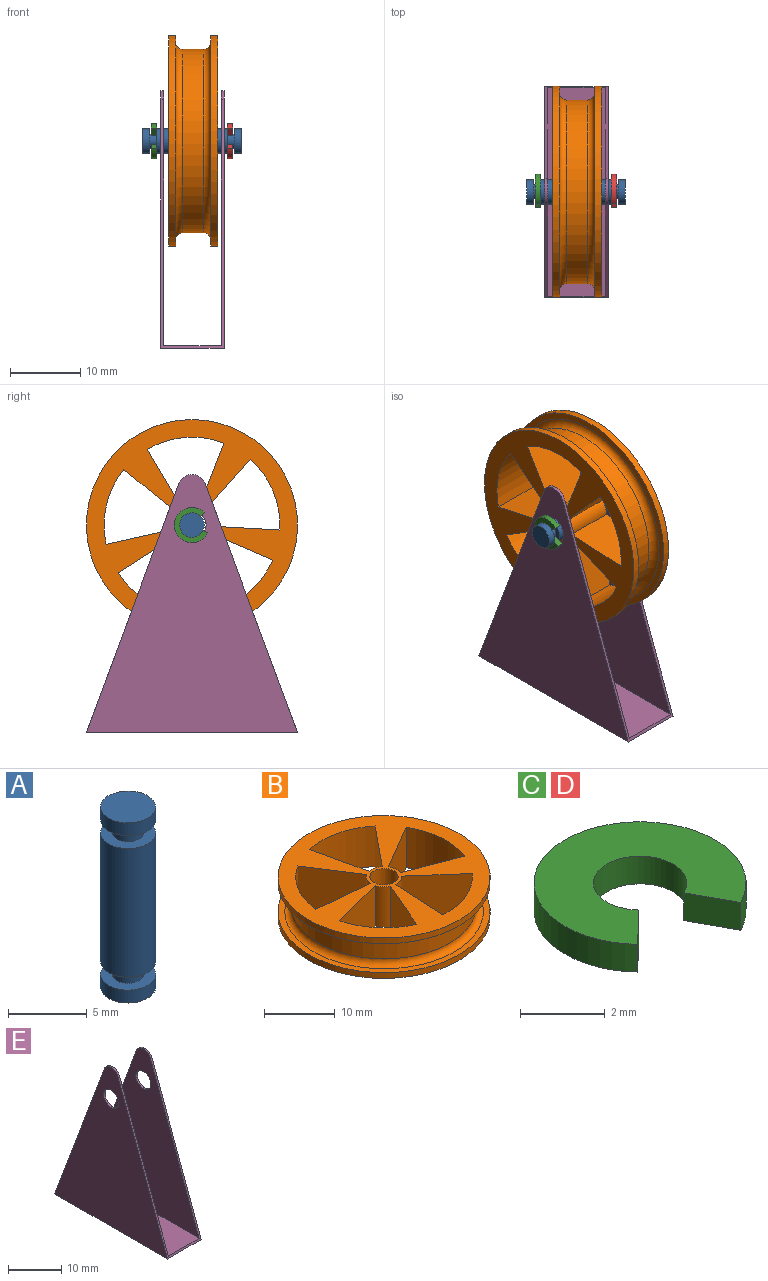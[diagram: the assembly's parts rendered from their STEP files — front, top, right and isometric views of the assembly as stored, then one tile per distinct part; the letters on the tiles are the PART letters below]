
ASSEMBLY  parts=5 mates=6
PART A: 11 faces, bbox 3.5x3.5x14 mm
  f0: cylinder r=1.75mm len=10mm, axis (0,0,-1), area 110mm2, adj f2,f7
  f1: cylinder r=1mm len=2mm, axis (0,0,1), area 6.3mm2, adj f2,f3
  f2: plane 3.5x3.5mm, normal (0,0,1), area 6.5mm2, adj f0,f1
  f3: plane 3.5x3.5mm, normal (0,0,-1), area 6.5mm2, adj f1,f5
  f4: plane 3.5x3.5mm, normal (0,0,1), area 9.6mm2, adj f5
  f5: cylinder r=1.75mm len=3.5mm, axis (0,0,-1), area 11mm2, adj f3,f4
  f6: cylinder r=1mm len=2mm, axis (0,0,-1), area 6.3mm2, adj f7,f8
  f7: plane 3.5x3.5mm, normal (0,0,-1), area 6.5mm2, adj f0,f6
  f8: plane 3.5x3.5mm, normal (0,0,1), area 6.5mm2, adj f6,f10
  f9: plane 3.5x3.5mm, normal (0,0,-1), area 9.6mm2, adj f10
  f10: cylinder r=1.75mm len=3.5mm, axis (0,0,-1), area 11mm2, adj f8,f9
PART B: 30 faces, bbox 31.9x31.9x7 mm
  f0: cylinder r=15mm len=30mm, axis (0,0,-1), area 94.2mm2, adj f23,f25
  f1: cylinder r=2.5mm len=7mm, axis (0,0,-1), area 15.8mm2, adj f2,f21,f22,f23
  f2: plane 7.5x7mm, normal (-0.66,-0.75,0), area 70mm2, adj f1,f3,f22,f23
  f3: cylinder r=12.5mm len=10.07mm, axis (0,0,-1), area 79.1mm2, adj f2,f21,f22,f23
  f4: cylinder r=2.5mm len=7mm, axis (0,0,-1), area 15.8mm2, adj f5,f16,f22,f23
  f5: plane 8.61x7mm, normal (0.51,-0.86,0), area 70mm2, adj f4,f6,f22,f23
  f6: cylinder r=12.5mm len=10.88mm, axis (0,0,-1), area 79.1mm2, adj f5,f16,f22,f23
  f7: cylinder r=12.5mm len=8.28mm, axis (0,0,-1), area 79.1mm2, adj f8,f17,f22,f23
  f8: plane 9.67x7mm, normal (0.26,-0.97,0), area 70mm2, adj f7,f9,f22,f23
  f9: cylinder r=2.5mm len=7mm, axis (0,0,-1), area 15.8mm2, adj f8,f17,f22,f23
  f10: cylinder r=2.5mm len=7mm, axis (0,0,-1), area 15.8mm2, adj f11,f19,f22,f23
  f11: plane 9.76x7mm, normal (0.98,0.22,0), area 70mm2, adj f10,f12,f22,f23
  f12: cylinder r=12.5mm len=10.63mm, axis (0,0,-1), area 79.1mm2, adj f11,f19,f22,f23
  f13: plane 8.41x7mm, normal (-0.84,-0.54,0), area 70mm2, adj f14,f20,f22,f23
  f14: cylinder r=2.5mm len=7mm, axis (0,0,-1), area 15.8mm2, adj f13,f15,f22,f23
  f15: plane 9.96x7mm, normal (0.09,1,0), area 70mm2, adj f14,f20,f22,f23
  f16: plane 9.32x7mm, normal (0.36,0.93,0), area 70mm2, adj f4,f6,f22,f23
  f17: plane 9.18x7mm, normal (-0.92,0.4,0), area 70mm2, adj f7,f9,f22,f23
  f18: cylinder r=15mm len=30mm, axis (0,0,-1), area 94.2mm2, adj f22,f26
  f19: plane 7.75x7mm, normal (-0.78,0.63,0), area 70mm2, adj f10,f12,f22,f23
  f20: cylinder r=12.5mm len=9.33mm, axis (0,0,-1), area 79.1mm2, adj f13,f15,f22,f23
  f21: plane 9.98x7mm, normal (1,-0.06,0), area 70mm2, adj f1,f3,f22,f23
  f22: plane 30x30mm, normal (0,0,1), area 355.3mm2, adj f1,f2,f3,f4,f5,f6,f7,f8
  f23: plane 30x30mm, normal (0,0,-1), area 355.3mm2, adj f0,f1,f2,f3,f4,f5,f6,f7
  f24: cylinder r=13.05mm len=26.1mm, axis (0,0,1), area 245.9mm2, adj f28,f29
  f25: plane 30x30mm, normal (0,0,1), area 86.9mm2, adj f0,f29
  f26: plane 30x30mm, normal (0,0,-1), area 86.9mm2, adj f18,f28
  f27: cylinder r=2mm len=7mm, axis (0,0,1), area 88mm2, adj f22,f23
  f28: torus R=14.05mm, axis (0,0,1), area 132.4mm2, adj f24,f26
  f29: torus R=14.05mm, axis (0,0,1), area 132.4mm2, adj f24,f25
PART C: 6 faces, bbox 5x4.7x0.8 mm
  f0: cylinder r=2.5mm len=5mm, axis (0,0,-1), area 10mm2, adj f1,f2,f4,f5
  f1: plane 5x4.74mm, normal (0,0,1), area 12.7mm2, adj f0,f3,f4,f5
  f2: plane 5x4.74mm, normal (0,0,-1), area 12.7mm2, adj f0,f3,f4,f5
  f3: cylinder r=1.1mm len=2.2mm, axis (0,0,1), area 4.4mm2, adj f1,f2,f4,f5
  f4: plane 1.01x0.97mm, normal (0.69,-0.72,0), area 1.1mm2, adj f0,f1,f2,f3
  f5: plane 1.23x0.8mm, normal (-0.88,-0.48,0), area 1.1mm2, adj f0,f1,f2,f3
PART D: same geometry as C
PART E: 12 faces, bbox 9x30x36.7 mm
  f0: plane 36.25x29.7mm, normal (-1,0,0), area 575.6mm2, adj f2,f3,f4,f5,f7
  f1: plane 36.25x29.7mm, normal (1,0,0), area 575.6mm2, adj f2,f3,f5,f6,f8
  f2: plane 29.7x8.2mm, normal (0,0,1), area 243.6mm2, adj f0,f1,f3,f5
  f3: plane 35.35x13.13mm, normal (0,0.94,0.35), area 33.7mm2, adj f0,f1,f2,f4,f6,f9,f10,f11
  f4: cylinder r=2mm len=3.75mm, axis (-1,0,0), area 1.9mm2, adj f0,f3,f5,f10
  f5: plane 35.35x13.13mm, normal (0,-0.94,0.35), area 33.7mm2, adj f0,f1,f2,f4,f6,f9,f10,f11
  f6: cylinder r=2mm len=3.75mm, axis (-1,0,0), area 1.9mm2, adj f1,f3,f5,f9
  f7: cylinder r=2mm len=4mm, axis (-1,0,0), area 5mm2, adj f0,f10
  f8: cylinder r=2mm len=4mm, axis (-1,0,0), area 5mm2, adj f1,f9
  f9: plane 36.65x30mm, normal (-1,0,0), area 587.5mm2, adj f3,f5,f6,f8,f11
  f10: plane 36.65x30mm, normal (1,0,0), area 587.5mm2, adj f3,f4,f5,f7,f11
  f11: plane 30x9mm, normal (0,0,-1), area 270mm2, adj f3,f5,f9,f10
PLACE A rot(axis=(-0.58,-0.58,0.58),120deg) t=(-4.21,-6.21,9.28)mm
PLACE B rot(axis=(0,-1,0),90deg) t=(-7.55,-6.21,9.28)mm
PLACE C rot(axis=(0,1,0),90deg) t=(-17.01,-6.21,15.86)mm
PLACE D rot(axis=(0,1,0),90deg) t=(-6.21,-6.21,15.86)mm
PLACE E t=(-7.64,-8.5,-20.18)mm
MATE planar A.f0 <-> C.f0  axis (-1,0,0) through (-16.21,-6.21,9.28)mm
MATE planar A.f0 <-> D.f2  axis (1,0,0) through (-6.21,-6.21,9.28)mm
MATE cylindrical A.f0 <-> B.f3  axis (1,0,0) through (-17.71,-6.21,9.28)mm
MATE cylindrical C.f0 <-> A.f0  axis (1,0,0) through (-16.21,-6.21,9.28)mm
MATE cylindrical D.f0 <-> A.f6  axis (1,0,0) through (-5.41,-6.21,9.28)mm
MATE cylindrical E.f7 <-> A.f0  axis (-1,0,0) through (-15.65,-6.21,9.28)mm
